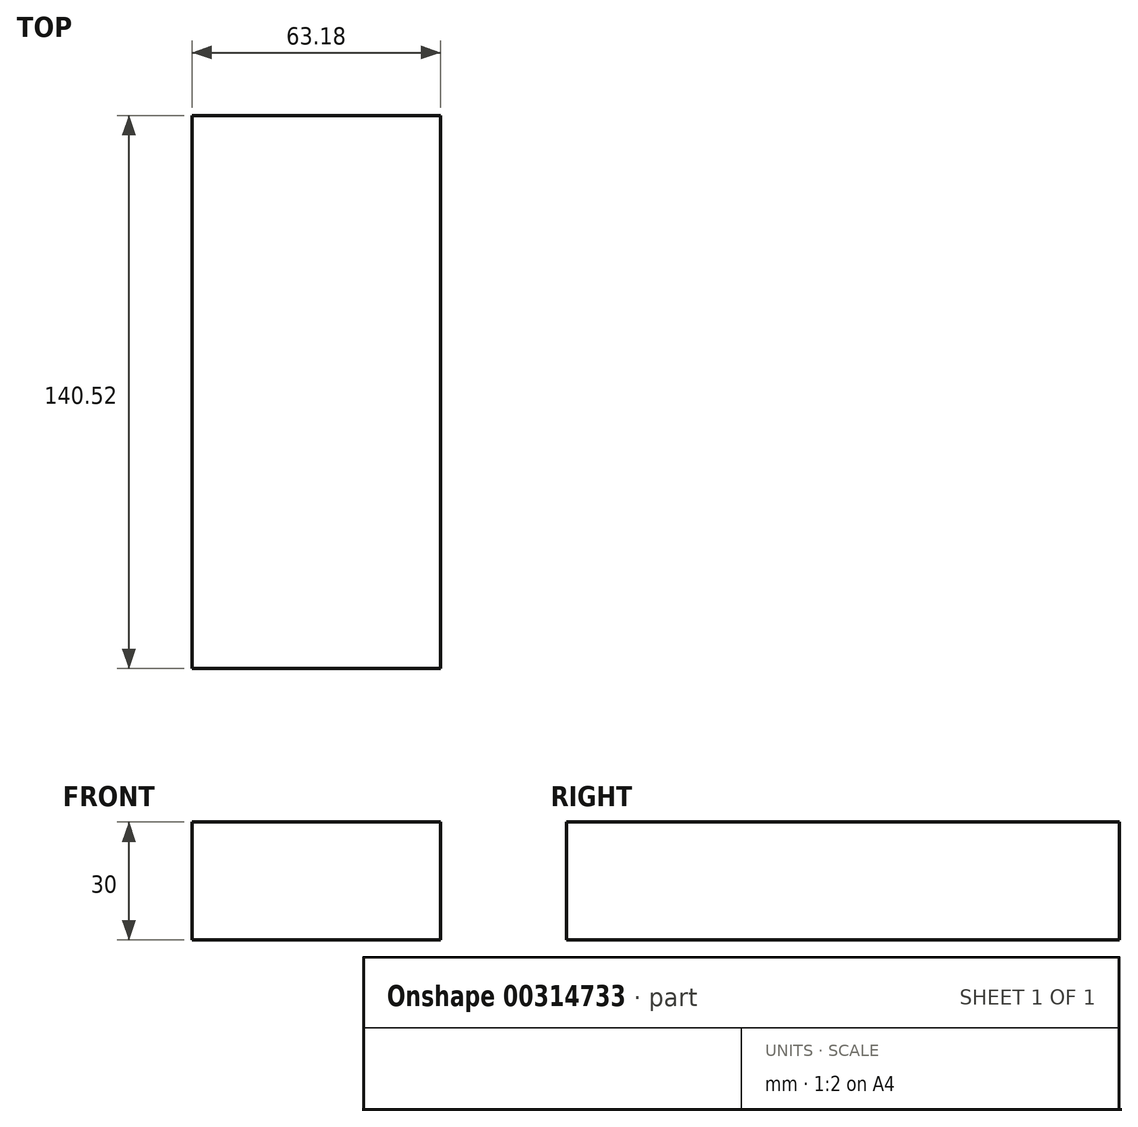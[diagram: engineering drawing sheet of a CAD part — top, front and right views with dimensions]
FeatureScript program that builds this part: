
annotation { "Feature Type Name" : "Feature", "Feature Type Description" : "" }
export const myFeature = defineFeature(function(context is Context, id is Id, definition is map)
    precondition{}
    {
        {
            var Q0;
            Q0=qCreatedBy(makeId("Top.planeOp"),FACE);
            var sketch = newSketch(context, id + "F0", { "sketchPlane" : qUnion([Q0])});
            skLineSegment(sketch, "E0.bottom", {"start": v(-31.59, 70.26) * mm, "end": v(31.59, 70.26) * mm});
            skLineSegment(sketch, "E0.top", {"start": v(-31.59, -70.26) * mm, "end": v(31.59, -70.26) * mm});
            skLineSegment(sketch, "E0.left", {"start": v(-31.59, 70.26) * mm, "end": v(-31.59, -70.26) * mm});
            skLineSegment(sketch, "E0.right", {"start": v(31.59, 70.26) * mm, "end": v(31.59, -70.26) * mm});
            skPoint(sketch, "E0.middle", {"position": v(0, 0) * mm});
            skSolve(sketch);
        }
        {
            var Q0;
            Q0=makeQuery(id+"F0.imprint","IMPRINT",FACE,{"disambiguationData":[TD([[makeQuery(id+"F0.imprint","IMPRINT",EDGE,{"derivedFrom":sQuery(id+"F0.wireOp",EDGE,"E0.bottom")}),-1.0]])]});
            extrude(context, id + "F1", {"entities" : qUnion([Q0]), "depth" : 30 * mm});
        }
    });
